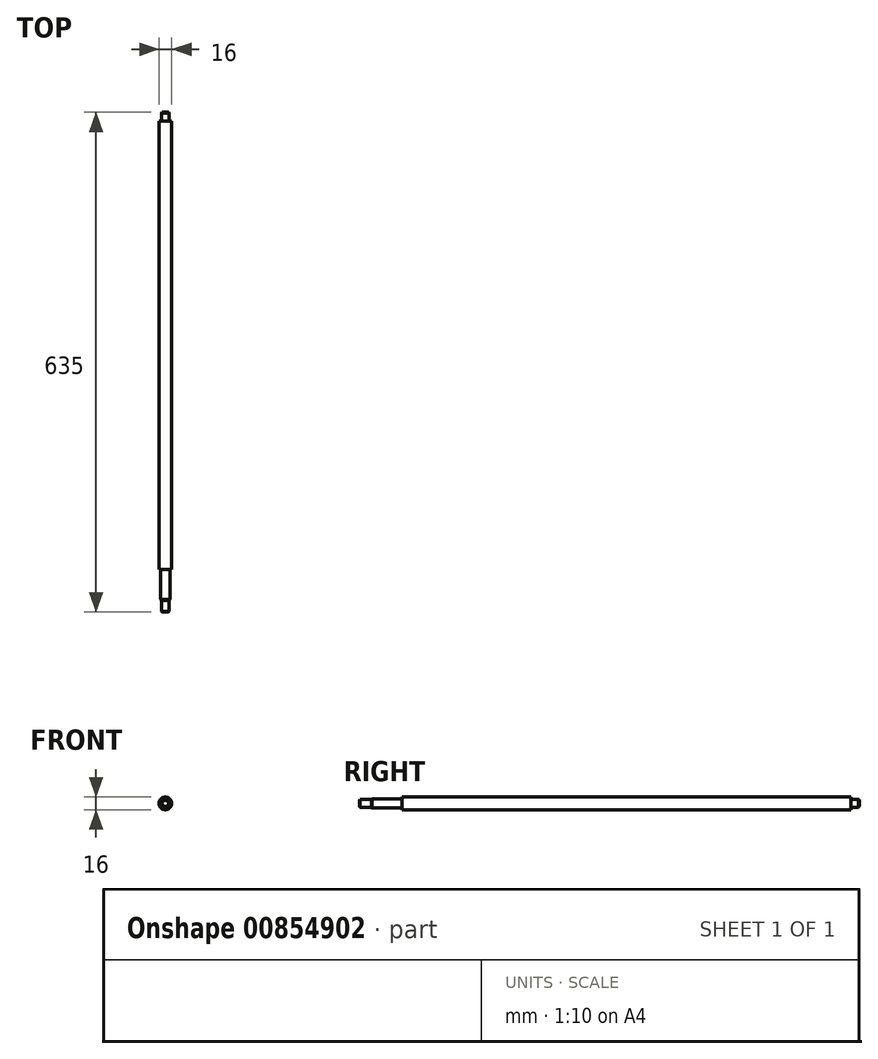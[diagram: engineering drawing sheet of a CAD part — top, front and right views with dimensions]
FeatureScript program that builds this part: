
annotation { "Feature Type Name" : "Feature", "Feature Type Description" : "" }
export const myFeature = defineFeature(function(context is Context, id is Id, definition is map)
    precondition{}
    {
        {
            var Q0;
            Q0=qCreatedBy(makeId("Right.planeOp"),FACE);
            var sketch = newSketch(context, id + "F0", { "sketchPlane" : qUnion([Q0])});
            skLineSegment(sketch, "E0", {"start": v(0, 0) * mm, "end": v(0, 5) * mm});
            skLineSegment(sketch, "E1", {"start": v(0, 5) * mm, "end": v(15, 5) * mm});
            skLineSegment(sketch, "E2", {"start": v(15, 5) * mm, "end": v(15, 6) * mm});
            skLineSegment(sketch, "E3", {"start": v(15, 6) * mm, "end": v(54, 6) * mm});
            skLineSegment(sketch, "E4", {"start": v(54, 8) * mm, "end": v(54, 6) * mm});
            skLineSegment(sketch, "E5", {"start": v(54, 8) * mm, "end": v(624, 8) * mm});
            skLineSegment(sketch, "E6", {"start": v(-5.84, 0) * mm, "end": v(694.16, 0) * mm, "construction": true});
            skLineSegment(sketch, "E7", {"start": v(624, 8) * mm, "end": v(624, 5) * mm});
            skLineSegment(sketch, "E8", {"start": v(624, 5) * mm, "end": v(635, 5) * mm});
            skLineSegment(sketch, "E9", {"start": v(635, 5) * mm, "end": v(635, 0) * mm});
            skLineSegment(sketch, "E10", {"start": v(635, 0) * mm, "end": v(0, 0) * mm});
            skSolve(sketch);
        }
        {
            var Q0;
            Q0 = qSketchRegion(id + "F0", true);
            var Q1;
            Q1=sQuery(id+"F0.wireOp",EDGE,"E6");
            revolve(context, id + "F1", {"surfaceOperationType" : NewSurfaceOperationType.NEW, "entities" : qUnion([Q0]), "axis" : qUnion([Q1]), "revolveType" : RevolveType.FULL});
        }
        {
            var Q0;
            Q0=makeQuery(id+"F1.opRevolve","SWEPT_EDGE",EDGE,{"disambiguationData":[OSD([sQuery(id+"F0.wireOp",EDGE,"E0"),sQuery(id+"F0.wireOp",EDGE,"E1")])]});
            var Q1;
            Q1=makeQuery(id+"F1.opRevolve","SWEPT_EDGE",EDGE,{"disambiguationData":[OSD([sQuery(id+"F0.wireOp",EDGE,"E2"),sQuery(id+"F0.wireOp",EDGE,"E3")])]});
            var Q2;
            Q2=makeQuery(id+"F1.opRevolve","SWEPT_EDGE",EDGE,{"disambiguationData":[OSD([sQuery(id+"F0.wireOp",EDGE,"E8"),sQuery(id+"F0.wireOp",EDGE,"E9")])]});
            chamfer(context, id + "F2", {"entities" : qUnion([Q0, Q1, Q2]), "width" : 1 * mm, "tangentPropagation" : true});
        }
    });
